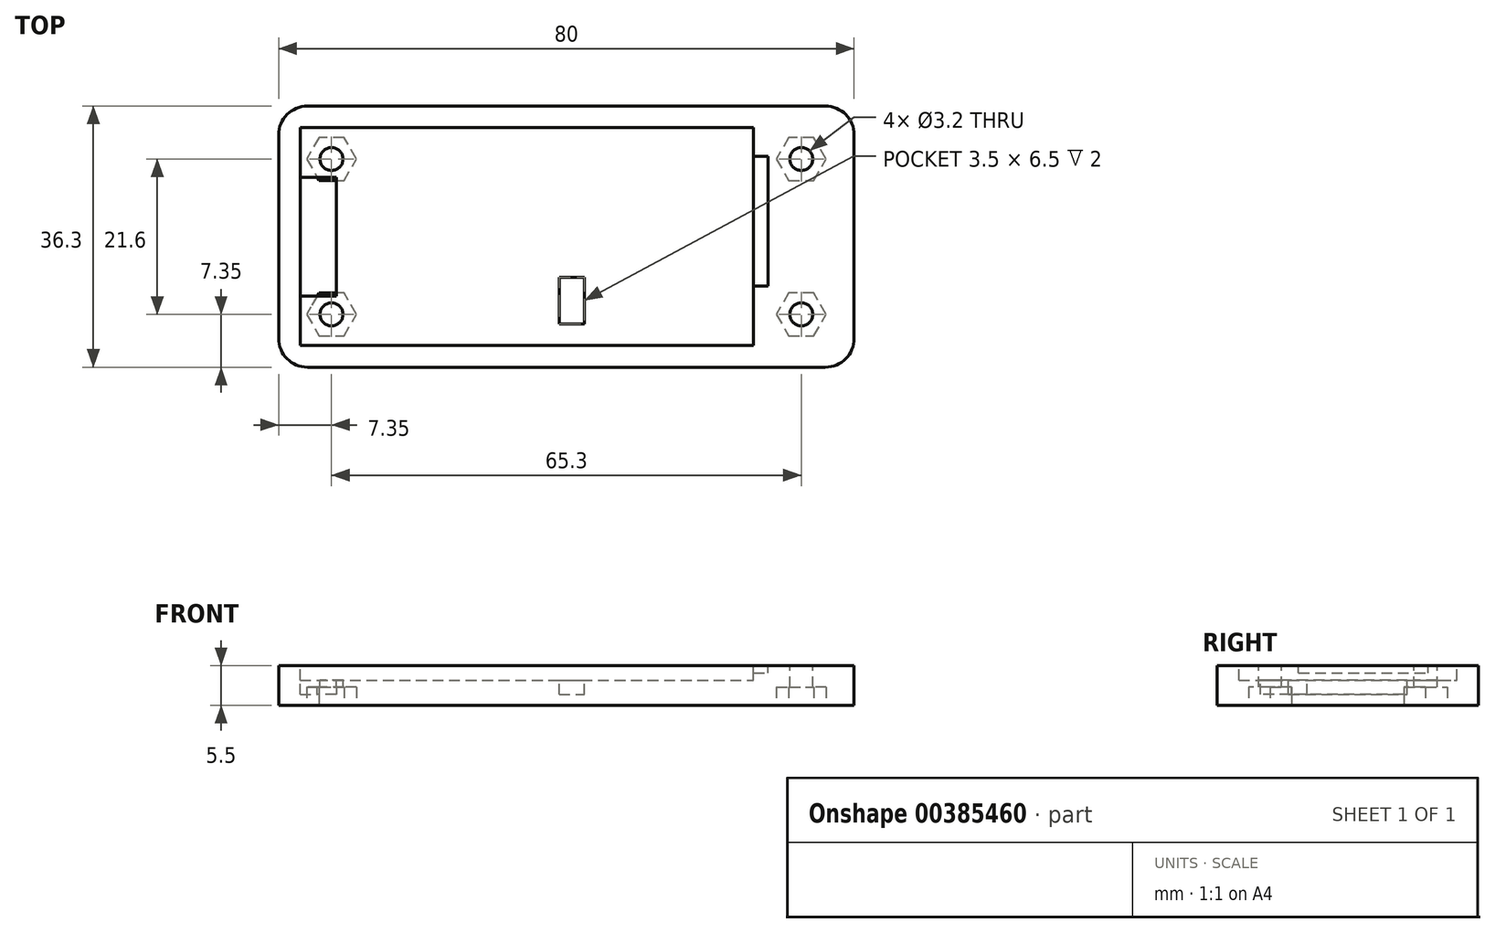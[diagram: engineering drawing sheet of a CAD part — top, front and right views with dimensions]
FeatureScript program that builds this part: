
annotation { "Feature Type Name" : "Feature", "Feature Type Description" : "" }
export const myFeature = defineFeature(function(context is Context, id is Id, definition is map)
    precondition{}
    {
        {
            var Q0;
            Q0=qCreatedBy(makeId("Top.planeOp"),FACE);
            var sketch = newSketch(context, id + "F0", { "sketchPlane" : qUnion([Q0])});
            skLineSegment(sketch, "E0.bottom", {"start": v(0, 0) * mm, "end": v(63, 0) * mm, "construction": true});
            skLineSegment(sketch, "E0.top", {"start": v(0, 30.3) * mm, "end": v(63, 30.3) * mm, "construction": true});
            skLineSegment(sketch, "E0.left", {"start": v(0, 0) * mm, "end": v(0, 30.3) * mm, "construction": true});
            skLineSegment(sketch, "E0.right", {"start": v(63, 0) * mm, "end": v(63, 30.3) * mm, "construction": true});
            skLineSegment(sketch, "E1.0", {"start": v(-3, 33.3) * mm, "end": v(77, 33.3) * mm});
            skLineSegment(sketch, "E1.1", {"start": v(-3, -3) * mm, "end": v(-3, 33.3) * mm});
            skLineSegment(sketch, "E1.2", {"start": v(-3, -3) * mm, "end": v(77, -3) * mm});
            skLineSegment(sketch, "E1.3", {"start": v(77, -3) * mm, "end": v(77, 33.3) * mm});
            skSolve(sketch);
        }
        {
            var Q0;
            Q0 = qSketchRegion(id + "F0", true);
            extrude(context, id + "F1", {"entities" : qUnion([Q0]), "depth" : 5.5 * mm});
        }
        {
            var Q0;
            Q0=makeQuery(id+"F1.opExtrude","SWEPT_EDGE",EDGE,{"disambiguationData":[OSD([sQuery(id+"F0.wireOp",EDGE,"E1.1"),sQuery(id+"F0.wireOp",EDGE,"E1.2")])]});
            var Q1;
            Q1=makeQuery(id+"F1.opExtrude","SWEPT_EDGE",EDGE,{"disambiguationData":[OSD([sQuery(id+"F0.wireOp",EDGE,"E1.2"),sQuery(id+"F0.wireOp",EDGE,"E1.3")])]});
            var Q2;
            Q2=makeQuery(id+"F1.opExtrude","SWEPT_EDGE",EDGE,{"disambiguationData":[OSD([sQuery(id+"F0.wireOp",EDGE,"E1.0"),sQuery(id+"F0.wireOp",EDGE,"E1.3")])]});
            var Q3;
            Q3=makeQuery(id+"F1.opExtrude","SWEPT_EDGE",EDGE,{"disambiguationData":[OSD([sQuery(id+"F0.wireOp",EDGE,"E1.0"),sQuery(id+"F0.wireOp",EDGE,"E1.1")])]});
            fillet(context, id + "F2", {"entities" : qUnion([Q0, Q1, Q2, Q3]), "radius" : 4 * mm, "tangentPropagation" : true, "allowEdgeOverflow" : false});
        }
        {
            var Q0;
            Q0=makeQuery(id+"F1.opExtrude","CAP_FACE",FACE,{"disambiguationData":[OSD([sQuery(id+"F0.wireOp",EDGE,"E1.0"),sQuery(id+"F0.wireOp",EDGE,"E1.1"),sQuery(id+"F0.wireOp",EDGE,"E1.2"),sQuery(id+"F0.wireOp",EDGE,"E1.3")])],"isStart":false});
            var sketch = newSketch(context, id + "F3", { "sketchPlane" : qUnion([Q0])});
            skLineSegment(sketch, "E2.bottom", {"start": v(0, 0) * mm, "end": v(63, 0) * mm});
            skLineSegment(sketch, "E2.top", {"start": v(0, 30.3) * mm, "end": v(63, 30.3) * mm});
            skLineSegment(sketch, "E2.left", {"start": v(0, 0) * mm, "end": v(0, 30.3) * mm});
            skLineSegment(sketch, "E2.right", {"start": v(63, 0) * mm, "end": v(63, 30.3) * mm});
            skSolve(sketch);
        }
        {
            var Q0;
            Q0 = qSketchRegion(id + "F3", true);
            extrude(context, id + "F4", {"entities" : qUnion([Q0]), "operationType" : NewBodyOperationType.REMOVE, "oppositeDirection" : true, "depth" : 2 * mm});
        }
        {
            var Q0;
            Q0=makeQuery(id+"F1.opExtrude","CAP_FACE",FACE,{"disambiguationData":[OSD([sQuery(id+"F0.wireOp",EDGE,"E1.0"),sQuery(id+"F0.wireOp",EDGE,"E1.1"),sQuery(id+"F0.wireOp",EDGE,"E1.2"),sQuery(id+"F0.wireOp",EDGE,"E1.3")])],"isStart":false});
            var sketch = newSketch(context, id + "F5", { "sketchPlane" : qUnion([Q0])});
            skLineSegment(sketch, "E3.bottom", {"start": v(0, 23.4) * mm, "end": v(5, 23.4) * mm});
            skLineSegment(sketch, "E3.top", {"start": v(0, 6.9) * mm, "end": v(5, 6.9) * mm});
            skLineSegment(sketch, "E3.left", {"start": v(0, 23.4) * mm, "end": v(0, 6.9) * mm});
            skLineSegment(sketch, "E3.right", {"start": v(5, 23.4) * mm, "end": v(5, 6.9) * mm});
            skLineSegment(sketch, "E4", {"start": v(0, 15.15) * mm, "end": v(5, 15.15) * mm, "construction": true});
            skLineSegment(sketch, "E5.bottom", {"start": v(36, 9.5) * mm, "end": v(39.5, 9.5) * mm});
            skLineSegment(sketch, "E5.top", {"start": v(36, 3) * mm, "end": v(39.5, 3) * mm});
            skLineSegment(sketch, "E5.left", {"start": v(36, 9.5) * mm, "end": v(36, 3) * mm});
            skLineSegment(sketch, "E5.right", {"start": v(39.5, 9.5) * mm, "end": v(39.5, 3) * mm});
            skSolve(sketch);
        }
        {
            var Q0;
            Q0 = qSketchRegion(id + "F5", true);
            extrude(context, id + "F6", {"entities" : qUnion([Q0]), "operationType" : NewBodyOperationType.REMOVE, "oppositeDirection" : true, "depth" : 4 * mm});
        }
        {
            var Q0;
            Q0=makeQuery(id+"F1.opExtrude","CAP_FACE",FACE,{"disambiguationData":[OSD([sQuery(id+"F0.wireOp",EDGE,"E1.0"),sQuery(id+"F0.wireOp",EDGE,"E1.1"),sQuery(id+"F0.wireOp",EDGE,"E1.2"),sQuery(id+"F0.wireOp",EDGE,"E1.3")])],"isStart":false});
            var sketch = newSketch(context, id + "F7", { "sketchPlane" : qUnion([Q0])});
            skLineSegment(sketch, "E6.bottom", {"start": v(63, 8.3) * mm, "end": v(65, 8.3) * mm});
            skLineSegment(sketch, "E6.top", {"start": v(63, 26.3) * mm, "end": v(65, 26.3) * mm});
            skLineSegment(sketch, "E6.left", {"start": v(63, 8.3) * mm, "end": v(63, 26.3) * mm});
            skLineSegment(sketch, "E6.right", {"start": v(65, 8.3) * mm, "end": v(65, 26.3) * mm});
            skSolve(sketch);
        }
        {
            var Q0;
            Q0 = qSketchRegion(id + "F7", true);
            extrude(context, id + "F8", {"entities" : qUnion([Q0]), "operationType" : NewBodyOperationType.REMOVE, "oppositeDirection" : true, "depth" : 1 * mm});
        }
        {
            var Q0;
            Q0=makeQuery(id+"F1.opExtrude","CAP_FACE",FACE,{"disambiguationData":[OSD([sQuery(id+"F0.wireOp",EDGE,"E1.0"),sQuery(id+"F0.wireOp",EDGE,"E1.1"),sQuery(id+"F0.wireOp",EDGE,"E1.2"),sQuery(id+"F0.wireOp",EDGE,"E1.3")])],"isStart":false});
            var sketch = newSketch(context, id + "F9", { "sketchPlane" : qUnion([Q0])});
            skCircle(sketch, "E7", {"center": v(4.35, 4.35) * mm, "radius": 1.6 * mm});
            skCircle(sketch, "E8", {"center": v(4.35, 25.95) * mm, "radius": 1.6 * mm});
            skLineSegment(sketch, "E9", {"start": v(4.35, 25.95) * mm, "end": v(4.35, 4.35) * mm, "construction": true});
            skLineSegment(sketch, "E10", {"start": v(0, 15.15) * mm, "end": v(4.35, 15.15) * mm, "construction": true});
            skCircle(sketch, "E11.1.0.0", {"center": v(69.65, 25.95) * mm, "radius": 1.6 * mm});
            skCircle(sketch, "E11.1.0.1", {"center": v(69.65, 4.35) * mm, "radius": 1.6 * mm});
            skLineSegment(sketch, "E11.direction1", {"start": v(4.35, 4.35) * mm, "end": v(69.65, 4.35) * mm, "construction": true});
            skSolve(sketch);
        }
        {
            var Q0;
            Q0 = qSketchRegion(id + "F9", true);
            extrude(context, id + "F10", {"entities" : qUnion([Q0]), "operationType" : NewBodyOperationType.REMOVE, "endBound" : BoundingType.THROUGH_ALL, "oppositeDirection" : true, "depth" : 25 * mm});
        }
        {
            var Q0;
            Q0=makeQuery(id+"F1.opExtrude","CAP_FACE",FACE,{"disambiguationData":[OSD([sQuery(id+"F0.wireOp",EDGE,"E1.0"),sQuery(id+"F0.wireOp",EDGE,"E1.1"),sQuery(id+"F0.wireOp",EDGE,"E1.2"),sQuery(id+"F0.wireOp",EDGE,"E1.3")])],"isStart":true});
            var sketch = newSketch(context, id + "F11", { "sketchPlane" : qUnion([Q0])});
            skCircle(sketch, "E12.cCircle", {"center": v(69.65, -25.95) * mm, "radius": 3 * mm, "construction": true});
            skLineSegment(sketch, "E12.0", {"start": v(71.38, -28.95) * mm, "end": v(67.92, -28.95) * mm});
            skLineSegment(sketch, "E12.1", {"start": v(67.92, -28.95) * mm, "end": v(66.19, -25.95) * mm});
            skLineSegment(sketch, "E12.2", {"start": v(66.19, -25.95) * mm, "end": v(67.92, -22.95) * mm});
            skLineSegment(sketch, "E12.3", {"start": v(67.92, -22.95) * mm, "end": v(71.38, -22.95) * mm});
            skLineSegment(sketch, "E12.4", {"start": v(71.38, -22.95) * mm, "end": v(73.11, -25.95) * mm});
            skLineSegment(sketch, "E12.5", {"start": v(73.11, -25.95) * mm, "end": v(71.38, -28.95) * mm});
            skPoint(sketch, "E12.0.midPoint", {"position": v(69.65, -28.95) * mm});
            skLineSegment(sketch, "E13.0.1.0", {"start": v(71.38, -1.35) * mm, "end": v(73.11, -4.35) * mm});
            skLineSegment(sketch, "E13.0.1.1", {"start": v(67.92, -1.35) * mm, "end": v(71.38, -1.35) * mm});
            skLineSegment(sketch, "E13.0.1.2", {"start": v(73.11, -4.35) * mm, "end": v(71.38, -7.35) * mm});
            skPoint(sketch, "E13.0.1.3", {"position": v(69.65, -7.35) * mm});
            skCircle(sketch, "E13.0.1.4", {"center": v(69.65, -4.35) * mm, "radius": 3 * mm, "construction": true});
            skLineSegment(sketch, "E13.0.1.5", {"start": v(67.92, -7.35) * mm, "end": v(66.19, -4.35) * mm});
            skLineSegment(sketch, "E13.0.1.6", {"start": v(66.19, -4.35) * mm, "end": v(67.92, -1.35) * mm});
            skLineSegment(sketch, "E13.0.1.7", {"start": v(71.38, -7.35) * mm, "end": v(67.92, -7.35) * mm});
            skLineSegment(sketch, "E13.1.0.0", {"start": v(6.08, -22.95) * mm, "end": v(7.81, -25.95) * mm});
            skLineSegment(sketch, "E13.1.0.1", {"start": v(2.62, -22.95) * mm, "end": v(6.08, -22.95) * mm});
            skLineSegment(sketch, "E13.1.0.2", {"start": v(7.81, -25.95) * mm, "end": v(6.08, -28.95) * mm});
            skPoint(sketch, "E13.1.0.3", {"position": v(4.35, -28.95) * mm});
            skCircle(sketch, "E13.1.0.4", {"center": v(4.35, -25.95) * mm, "radius": 3 * mm, "construction": true});
            skLineSegment(sketch, "E13.1.0.5", {"start": v(2.62, -28.95) * mm, "end": v(0.89, -25.95) * mm});
            skLineSegment(sketch, "E13.1.0.6", {"start": v(0.89, -25.95) * mm, "end": v(2.62, -22.95) * mm});
            skLineSegment(sketch, "E13.1.0.7", {"start": v(6.08, -28.95) * mm, "end": v(2.62, -28.95) * mm});
            skLineSegment(sketch, "E13.1.1.0", {"start": v(6.08, -1.35) * mm, "end": v(7.81, -4.35) * mm});
            skLineSegment(sketch, "E13.1.1.1", {"start": v(2.62, -1.35) * mm, "end": v(6.08, -1.35) * mm});
            skLineSegment(sketch, "E13.1.1.2", {"start": v(7.81, -4.35) * mm, "end": v(6.08, -7.35) * mm});
            skPoint(sketch, "E13.1.1.3", {"position": v(4.35, -7.35) * mm});
            skCircle(sketch, "E13.1.1.4", {"center": v(4.35, -4.35) * mm, "radius": 3 * mm, "construction": true});
            skLineSegment(sketch, "E13.1.1.5", {"start": v(2.62, -7.35) * mm, "end": v(0.89, -4.35) * mm});
            skLineSegment(sketch, "E13.1.1.6", {"start": v(0.89, -4.35) * mm, "end": v(2.62, -1.35) * mm});
            skLineSegment(sketch, "E13.1.1.7", {"start": v(6.08, -7.35) * mm, "end": v(2.62, -7.35) * mm});
            skLineSegment(sketch, "E13.direction1", {"start": v(67.92, -28.95) * mm, "end": v(2.62, -28.95) * mm, "construction": true});
            skLineSegment(sketch, "E13.direction2", {"start": v(67.92, -28.95) * mm, "end": v(67.92, -7.35) * mm, "construction": true});
            skSolve(sketch);
        }
        {
            var Q0;
            Q0 = qSketchRegion(id + "F11", true);
            extrude(context, id + "F12", {"entities" : qUnion([Q0]), "operationType" : NewBodyOperationType.REMOVE, "oppositeDirection" : true, "depth" : 2.5 * mm});
        }
    });
